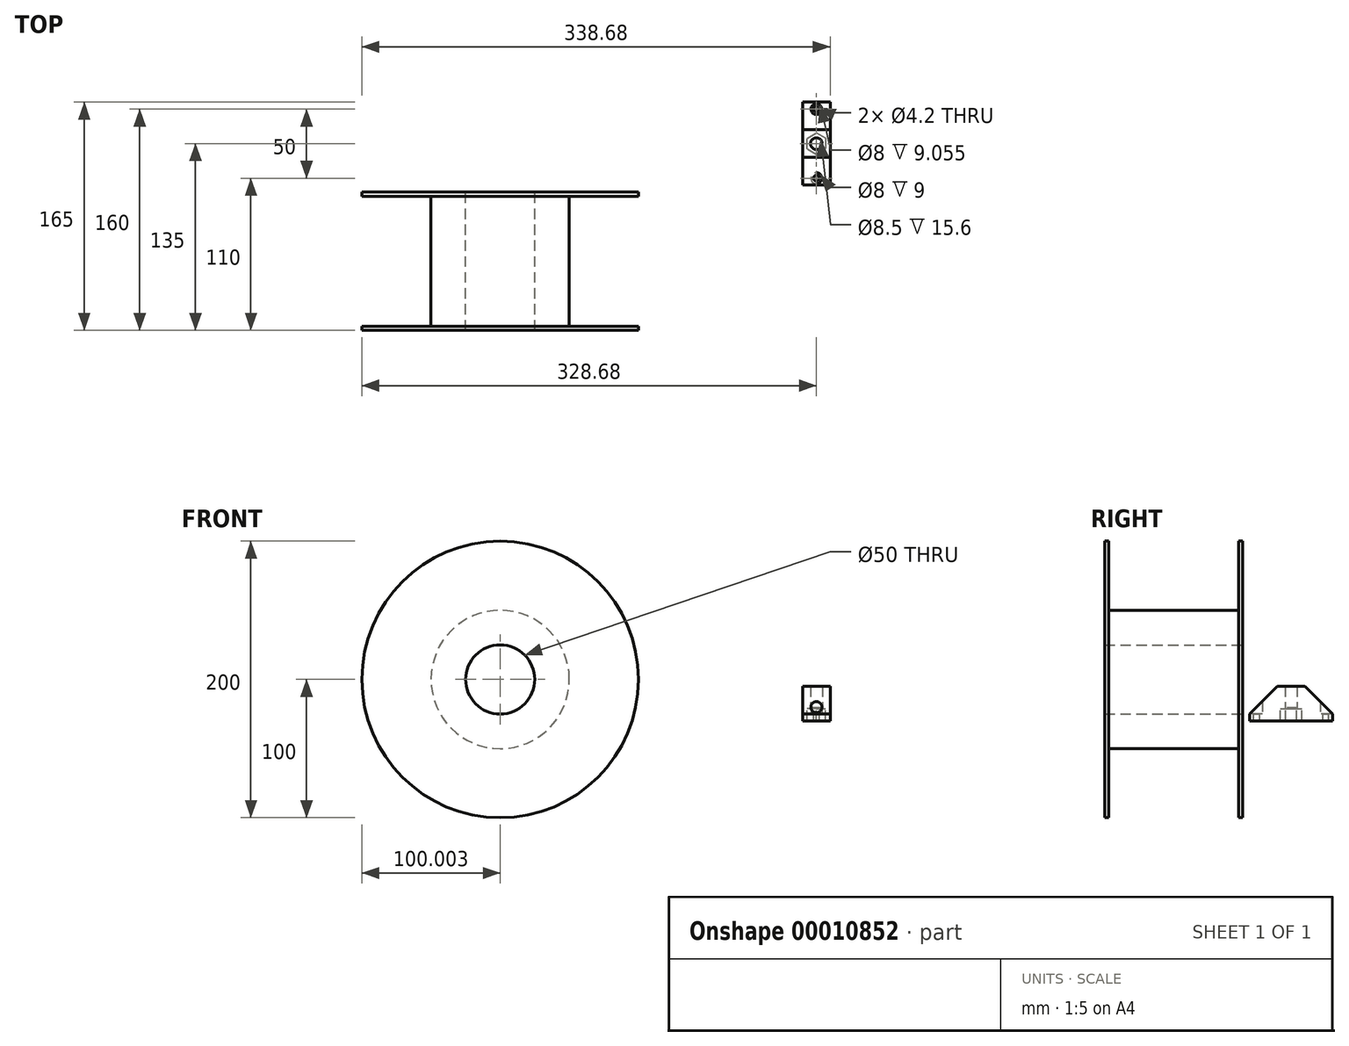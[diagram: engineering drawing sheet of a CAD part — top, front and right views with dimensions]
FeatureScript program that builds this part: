
annotation { "Feature Type Name" : "Feature", "Feature Type Description" : "" }
export const myFeature = defineFeature(function(context is Context, id is Id, definition is map)
    precondition{}
    {
        {
            var Q0;
            Q0=qCreatedBy(makeId("Front.planeOp"),FACE);
            var sketch = newSketch(context, id + "F0", { "sketchPlane" : qUnion([Q0])});
            skLineSegment(sketch, "E0.rect.bottom", {"start": v(-10, 30) * mm, "end": v(10, 30) * mm});
            skLineSegment(sketch, "E0.rect.top", {"start": v(-10, -30) * mm, "end": v(10, -30) * mm});
            skLineSegment(sketch, "E0.rect.left", {"start": v(-10, 30) * mm, "end": v(-10, -30) * mm});
            skLineSegment(sketch, "E0.rect.right", {"start": v(10, 30) * mm, "end": v(10, -30) * mm});
            skPoint(sketch, "E0.rect.middle", {"position": v(0, 0) * mm});
            skCircle(sketch, "E1.cCircle", {"center": v(0, 0) * mm, "radius": 6.75 * mm, "construction": true});
            skLineSegment(sketch, "E1.0", {"start": v(-6.75, -3.9) * mm, "end": v(-6.75, 3.9) * mm});
            skLineSegment(sketch, "E1.1", {"start": v(-6.75, 3.9) * mm, "end": v(0, 7.8) * mm});
            skLineSegment(sketch, "E1.2", {"start": v(0, 7.8) * mm, "end": v(6.75, 3.9) * mm});
            skLineSegment(sketch, "E1.3", {"start": v(6.75, 3.9) * mm, "end": v(6.75, -3.9) * mm});
            skLineSegment(sketch, "E1.4", {"start": v(6.75, -3.9) * mm, "end": v(0, -7.8) * mm});
            skLineSegment(sketch, "E1.5", {"start": v(0, -7.8) * mm, "end": v(-6.75, -3.9) * mm});
            skPoint(sketch, "E1.0.midPoint", {"position": v(-6.75, 0) * mm});
            skCircle(sketch, "E2", {"center": v(0, 25) * mm, "radius": 2.1 * mm});
            skCircle(sketch, "E3", {"center": v(0, -25) * mm, "radius": 2.1 * mm});
            skSolve(sketch);
        }
        {
            var Q0;
            Q0=makeQuery(id+"F0.imprint","IMPRINT",FACE,{"disambiguationData":[TD([[makeQuery(id+"F0.imprint","IMPRINT",EDGE,{"derivedFrom":sQuery(id+"F0.wireOp",EDGE,"E0.rect.bottom")}),-1.0]])]});
            var Q1;
            Q1=makeQuery(id+"F0.imprint","IMPRINT",FACE,{"disambiguationData":[TD([[makeQuery(id+"F0.imprint","IMPRINT",EDGE,{"derivedFrom":sQuery(id+"F0.wireOp",EDGE,"E2")}),1.0]])]});
            var Q2;
            Q2=makeQuery(id+"F0.imprint","IMPRINT",FACE,{"disambiguationData":[TD([[makeQuery(id+"F0.imprint","IMPRINT",EDGE,{"derivedFrom":sQuery(id+"F0.wireOp",EDGE,"E1.0")}),-1.0]])]});
            var Q3;
            Q3=makeQuery(id+"F0.imprint","IMPRINT",FACE,{"disambiguationData":[TD([[makeQuery(id+"F0.imprint","IMPRINT",EDGE,{"derivedFrom":sQuery(id+"F0.wireOp",EDGE,"E3")}),1.0]])]});
            extrude(context, id + "F1", {"entities" : qUnion([Q0, Q1, Q2, Q3]), "depth" : 20 * mm});
        }
        {
            var Q0;
            Q0=makeQuery(id+"F1.opExtrude","CAP_EDGE",EDGE,{"disambiguationData":[OSD([sQuery(id+"F0.wireOp",EDGE,"E0.rect.top")])],"isStart":false});
            var Q1;
            Q1=makeQuery(id+"F1.opExtrude","CAP_EDGE",EDGE,{"disambiguationData":[OSD([sQuery(id+"F0.wireOp",EDGE,"E0.rect.bottom")])],"isStart":false});
            chamfer(context, id + "F2", {"entities" : qUnion([Q0, Q1]), "chamferType" : ChamferType.TWO_OFFSETS, "width1" : 20 * mm, "oppositeDirection" : false, "width2" : 20 * mm, "tangentPropagation" : true});
        }
        {
            var Q0;
            Q0 = qSketchRegion(id + "F0", true);
            extrude(context, id + "F3", {"entities" : qUnion([Q0]), "operationType" : NewBodyOperationType.ADD, "oppositeDirection" : true, "depth" : 5 * mm});
        }
        {
            var Q0;
            Q0=makeQuery(id+"F3.boolean.opBoolean","SPLIT",FACE,{"disambiguationData":[TD([makeQuery(id+"F3.opExtrude","SWEPT_FACE",FACE,{"disambiguationData":[OSD([sQuery(id+"F0.wireOp",EDGE,"E1.0")])]})])],"derivedFrom":makeQuery(id+"F1.opExtrude","CAP_FACE",FACE,{"disambiguationData":[OSD([sQuery(id+"F0.wireOp",EDGE,"E0.rect.bottom"),sQuery(id+"F0.wireOp",EDGE,"E0.rect.top"),sQuery(id+"F0.wireOp",EDGE,"E0.rect.left"),sQuery(id+"F0.wireOp",EDGE,"E0.rect.right")])],"isStart":true})});
            extrude(context, id + "F4", {"entities" : qUnion([Q0]), "operationType" : NewBodyOperationType.REMOVE, "oppositeDirection" : true, "depth" : 4 * mm});
        }
        {
            var Q0;
            Q0=makeQuery(id+"F3.boolean.opBoolean","SPLIT",FACE,{"disambiguationData":[TD([makeQuery(id+"F3.opExtrude","SWEPT_FACE",FACE,{"disambiguationData":[OSD([sQuery(id+"F0.wireOp",EDGE,"E3")])]})])],"derivedFrom":makeQuery(id+"F1.opExtrude","CAP_FACE",FACE,{"disambiguationData":[OSD([sQuery(id+"F0.wireOp",EDGE,"E0.rect.bottom"),sQuery(id+"F0.wireOp",EDGE,"E0.rect.top"),sQuery(id+"F0.wireOp",EDGE,"E0.rect.left"),sQuery(id+"F0.wireOp",EDGE,"E0.rect.right")])],"isStart":true})});
            var sketch = newSketch(context, id + "F5", { "sketchPlane" : qUnion([Q0])});
            skCircle(sketch, "E4", {"center": v(0, -25) * mm, "radius": 4 * mm});
            skCircle(sketch, "E5", {"center": v(0, 25) * mm, "radius": 4 * mm});
            skSolve(sketch);
        }
        {
            var Q0;
            Q0 = qSketchRegion(id + "F5", true);
            extrude(context, id + "F6", {"entities" : qUnion([Q0]), "operationType" : NewBodyOperationType.REMOVE, "oppositeDirection" : true, "depth" : 25 * mm});
        }
        {
            var Q0;
            Q0=makeQuery(id+"F4.boolean.opBoolean","COPY",FACE,{"derivedFrom":makeQuery(id+"F4.opExtrude","CAP_FACE",FACE,{"disambiguationData":[OSD([sQuery(id+"F0.wireOp",EDGE,"E0.rect.bottom"),sQuery(id+"F0.wireOp",EDGE,"E0.rect.top"),sQuery(id+"F0.wireOp",EDGE,"E0.rect.left"),sQuery(id+"F0.wireOp",EDGE,"E0.rect.right")])],"isStart":false})});
            var sketch = newSketch(context, id + "F7", { "sketchPlane" : qUnion([Q0])});
            skCircle(sketch, "E6", {"center": v(0, 0) * mm, "radius": 4.25 * mm});
            skSolve(sketch);
        }
        {
            var Q0;
            Q0 = qSketchRegion(id + "F7", true);
            var Q1;
            Q1=makeQuery(id+"F1.opExtrude","CAP_FACE",FACE,{"disambiguationData":[OSD([sQuery(id+"F0.wireOp",EDGE,"E0.rect.bottom"),sQuery(id+"F0.wireOp",EDGE,"E0.rect.top"),sQuery(id+"F0.wireOp",EDGE,"E0.rect.left"),sQuery(id+"F0.wireOp",EDGE,"E0.rect.right")])],"isStart":false});
            extrude(context, id + "F8", {"entities" : qUnion([Q0]), "operationType" : NewBodyOperationType.REMOVE, "endBound" : BoundingType.UP_TO_SURFACE, "oppositeDirection" : true, "endBoundEntityFace" : qUnion([Q1]), "depth" : 25 * mm, "hasSecondDirection" : true, "secondDirectionOppositeDirection" : true, "secondDirectionDepth" : 0.4 * mm});
        }
        {
            var Q0;
            Q0=qCreatedBy(makeId("Front.planeOp"),FACE);
            var sketch = newSketch(context, id + "F9", { "sketchPlane" : qUnion([Q0])});
            skCircle(sketch, "E7", {"center": v(-228.68, 0) * mm, "radius": 100 * mm});
            skCircle(sketch, "E8", {"center": v(-228.68, 0) * mm, "radius": 25 * mm});
            skCircle(sketch, "E9", {"center": v(-228.68, 0) * mm, "radius": 50 * mm});
            skSolve(sketch);
        }
        {
            var Q0;
            Q0=makeQuery(id+"F9.imprint","IMPRINT",FACE,{"disambiguationData":[TD([[makeQuery(id+"F9.imprint","IMPRINT",EDGE,{"derivedFrom":sQuery(id+"F9.wireOp",EDGE,"E7")}),1.0]])]});
            extrude(context, id + "F10", {"entities" : qUnion([Q0]), "depth" : 3 * mm});
        }
        {
            var Q0;
            Q0=makeQuery(id+"F9.imprint","IMPRINT",FACE,{"disambiguationData":[TD([[makeQuery(id+"F9.imprint","IMPRINT",EDGE,{"derivedFrom":sQuery(id+"F9.wireOp",EDGE,"E8")}),-1.0]])]});
            extrude(context, id + "F11", {"entities" : qUnion([Q0]), "operationType" : NewBodyOperationType.ADD, "depth" : 100 * mm});
        }
        {
            var Q0;
            Q0=makeQuery(id+"F10.opExtrude","CAP_FACE",FACE,{"disambiguationData":[OSD([sQuery(id+"F9.wireOp",EDGE,"E7"),sQuery(id+"F9.wireOp",EDGE,"E9")])],"isStart":false});
            extrude(context, id + "F12", {"entities" : qUnion([Q0]), "operationType" : NewBodyOperationType.ADD, "depth" : 97 * mm, "hasSecondDirection" : true, "secondDirectionOppositeDirection" : false, "secondDirectionDepth" : 94 * mm});
        }
        {
            var Q0;
            Q0=makeQuery(id+"F1.opExtrude","SWEPT_BODY",BODY,{"disambiguationData":[OSD([sQuery(id+"F0.wireOp",EDGE,"E0.rect.bottom"),sQuery(id+"F0.wireOp",EDGE,"E0.rect.top"),sQuery(id+"F0.wireOp",EDGE,"E0.rect.left"),sQuery(id+"F0.wireOp",EDGE,"E0.rect.right")])]});
            var Q1;
            Q1=makeQuery(id+"F3.opExtrude","CAP_EDGE",EDGE,{"disambiguationData":[OSD([sQuery(id+"F0.wireOp",EDGE,"E0.rect.top")])],"isStart":false});
            transform(context, id + "F13", {"entities" : qUnion([Q0]), "transformType" : TransformType.ROTATION, "transformAxis" : qUnion([Q1]), "angle" : 90 * degree, "oppositeDirection" : true, "makeCopy" : false});
        }
    });
